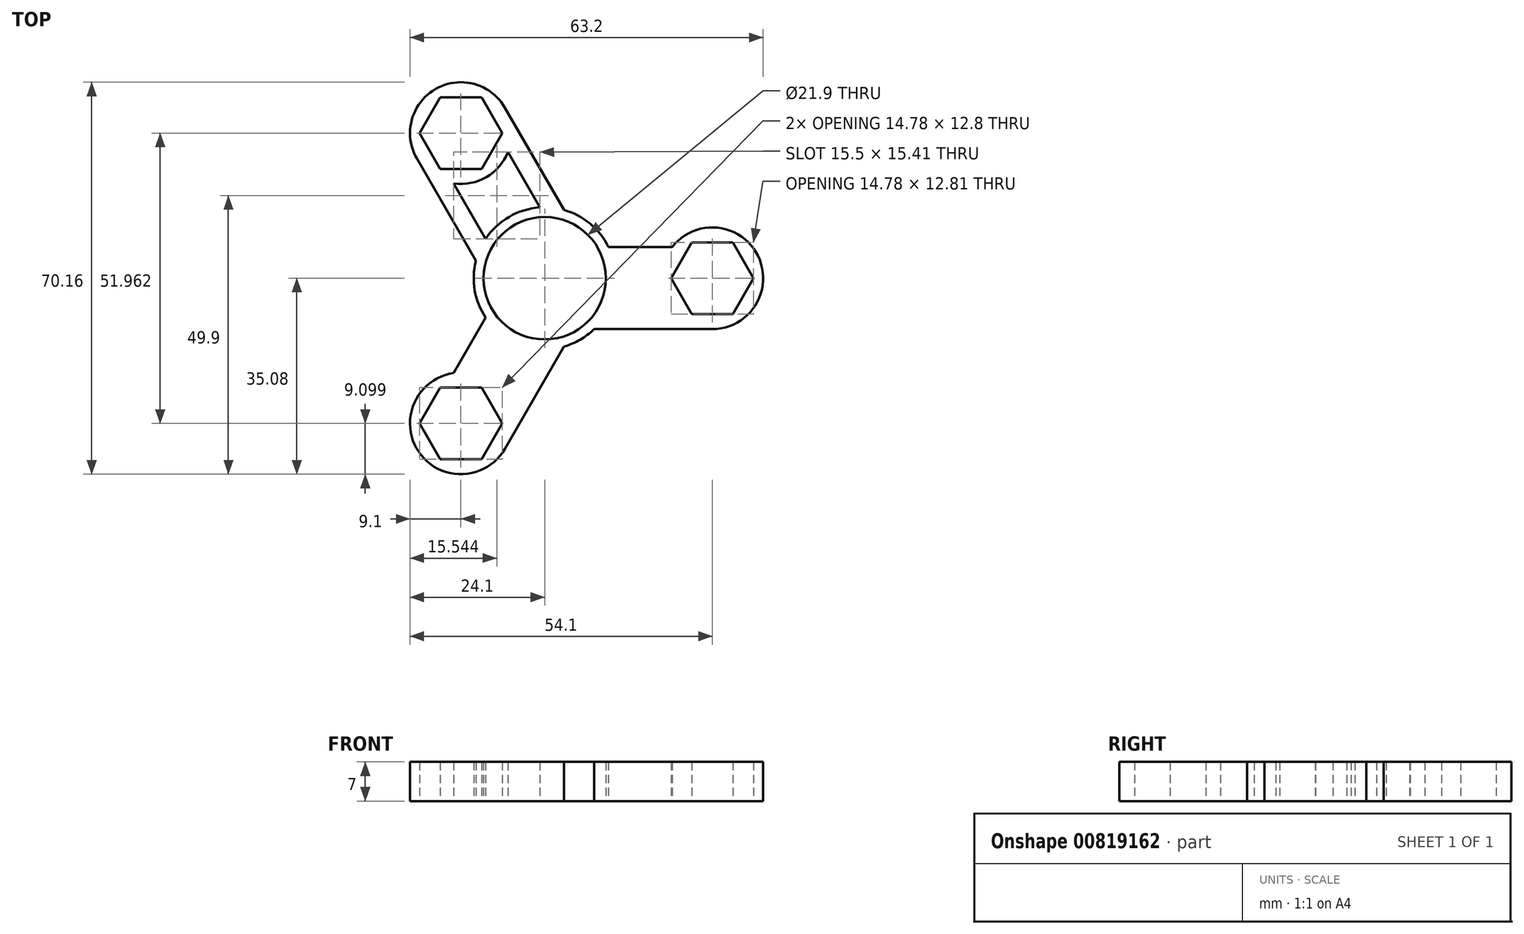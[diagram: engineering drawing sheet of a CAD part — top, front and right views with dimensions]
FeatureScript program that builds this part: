
annotation { "Feature Type Name" : "Feature", "Feature Type Description" : "" }
export const myFeature = defineFeature(function(context is Context, id is Id, definition is map)
    precondition{}
    {
        {
            var Q0;
            Q0=qCreatedBy(makeId("Top.planeOp"),FACE);
            var sketch = newSketch(context, id + "F0", { "sketchPlane" : qUnion([Q0])});
            skCircle(sketch, "E0", {"center": v(0, 0) * mm, "radius": 10.95 * mm});
            skCircle(sketch, "E1", {"center": v(0, 0) * mm, "radius": 12.7 * mm});
            skLineSegment(sketch, "E2", {"start": v(0, 0) * mm, "end": v(30, 0) * mm, "construction": true});
            skLineSegment(sketch, "E3", {"start": v(0, 0) * mm, "end": v(-15, -25.98) * mm, "construction": true});
            skLineSegment(sketch, "E4", {"start": v(0, 0) * mm, "end": v(-15, 25.98) * mm, "construction": true});
            skCircle(sketch, "E5.cCircle", {"center": v(-15, 25.98) * mm, "radius": 6.4 * mm, "construction": true});
            skLineSegment(sketch, "E5.0", {"start": v(-11.3, 32.38) * mm, "end": v(-7.6, 25.98) * mm});
            skLineSegment(sketch, "E5.1", {"start": v(-7.6, 25.98) * mm, "end": v(-11.3, 19.58) * mm});
            skLineSegment(sketch, "E5.2", {"start": v(-11.3, 19.58) * mm, "end": v(-18.7, 19.58) * mm});
            skLineSegment(sketch, "E5.3", {"start": v(-18.7, 19.58) * mm, "end": v(-22.4, 25.98) * mm});
            skLineSegment(sketch, "E5.4", {"start": v(-22.4, 25.98) * mm, "end": v(-18.7, 32.38) * mm});
            skLineSegment(sketch, "E5.5", {"start": v(-18.7, 32.38) * mm, "end": v(-11.3, 32.38) * mm});
            skPoint(sketch, "E5.0.midPoint", {"position": v(-9.46, 29.18) * mm});
            skCircle(sketch, "E6.cCircle", {"center": v(30, 0) * mm, "radius": 6.4 * mm, "construction": true});
            skLineSegment(sketch, "E6.0", {"start": v(26.3, -6.4) * mm, "end": v(22.6, 0.01) * mm});
            skLineSegment(sketch, "E6.1", {"start": v(22.6, 0.01) * mm, "end": v(26.32, 6.4) * mm});
            skLineSegment(sketch, "E6.2", {"start": v(26.32, 6.4) * mm, "end": v(33.7, 6.4) * mm});
            skLineSegment(sketch, "E6.3", {"start": v(33.7, 6.4) * mm, "end": v(37.4, -0.01) * mm});
            skLineSegment(sketch, "E6.4", {"start": v(37.4, -0.01) * mm, "end": v(33.68, -6.4) * mm});
            skLineSegment(sketch, "E6.5", {"start": v(33.68, -6.4) * mm, "end": v(26.3, -6.4) * mm});
            skPoint(sketch, "E6.0.midPoint", {"position": v(24.45, -3.19) * mm});
            skCircle(sketch, "E7.cCircle", {"center": v(-15, -25.98) * mm, "radius": 6.4 * mm, "construction": true});
            skLineSegment(sketch, "E7.0", {"start": v(-11.3, -19.58) * mm, "end": v(-7.6, -25.98) * mm});
            skLineSegment(sketch, "E7.1", {"start": v(-7.6, -25.98) * mm, "end": v(-11.3, -32.38) * mm});
            skLineSegment(sketch, "E7.2", {"start": v(-11.3, -32.38) * mm, "end": v(-18.7, -32.38) * mm});
            skLineSegment(sketch, "E7.3", {"start": v(-18.7, -32.38) * mm, "end": v(-22.4, -25.98) * mm});
            skLineSegment(sketch, "E7.4", {"start": v(-22.4, -25.98) * mm, "end": v(-18.7, -19.58) * mm});
            skLineSegment(sketch, "E7.5", {"start": v(-18.7, -19.58) * mm, "end": v(-11.3, -19.58) * mm});
            skPoint(sketch, "E7.0.midPoint", {"position": v(-9.46, -22.78) * mm});
            skCircle(sketch, "E8", {"center": v(-15, 25.98) * mm, "radius": 9.1 * mm});
            skCircle(sketch, "E9", {"center": v(30, 0) * mm, "radius": 9.1 * mm});
            skCircle(sketch, "E10", {"center": v(-15, -25.98) * mm, "radius": 9.1 * mm});
            skLineSegment(sketch, "E11.bottom", {"start": v(0, 9.1) * mm, "end": v(1.21, 9.1) * mm});
            skLineSegment(sketch, "E11.top", {"start": v(0, -9.1) * mm, "end": v(30.02, -9.1) * mm});
            skLineSegment(sketch, "E11.left", {"start": v(0, 9.1) * mm, "end": v(0, -9.1) * mm});
            skLineSegment(sketch, "E12.bottom", {"start": v(-7.12, 30.53) * mm, "end": v(3.45, 12.22) * mm});
            skLineSegment(sketch, "E12.top", {"start": v(-22.9, 21.47) * mm, "end": v(-7.9, -4.52) * mm});
            skLineSegment(sketch, "E12.right", {"start": v(7.86, 4.58) * mm, "end": v(-7.9, -4.52) * mm});
            skLineSegment(sketch, "E13.bottom", {"start": v(-22.88, -21.43) * mm, "end": v(-7.77, 4.75) * mm});
            skLineSegment(sketch, "E13.top", {"start": v(-7.14, -30.57) * mm, "end": v(8, -4.35) * mm});
            skLineSegment(sketch, "E13.right", {"start": v(-7.77, 4.75) * mm, "end": v(8, -4.35) * mm});
            skPoint(sketch, "E14", {"position": v(-7.12, 30.53) * mm});
            skPoint(sketch, "E15", {"position": v(30, 9.1) * mm});
            skPoint(sketch, "E16", {"position": v(-22.88, -21.43) * mm});
            skLineSegment(sketch, "E17.0", {"start": v(-10.15, 28.78) * mm, "end": v(4.83, 2.83) * mm});
            skLineSegment(sketch, "E18.0", {"start": v(-19.87, 23.22) * mm, "end": v(-4.87, -2.77) * mm});
            skLineSegment(sketch, "E19.0", {"start": v(-19.85, -23.18) * mm, "end": v(-4.74, 3) * mm});
            skLineSegment(sketch, "E20.0", {"start": v(-10.17, -28.82) * mm, "end": v(4.96, -2.6) * mm});
            skLineSegment(sketch, "E21.0", {"start": v(0, -5.6) * mm, "end": v(30.02, -5.6) * mm});
            skLineSegment(sketch, "E22.0", {"start": v(0, 5.6) * mm, "end": v(30, 5.6) * mm});
            skLineSegment(sketch, "E23.trimOffspring", {"start": v(7.27, 5.6) * mm, "end": v(7.86, 4.58) * mm});
            skLineSegment(sketch, "E24.trimOffspring", {"start": v(5.25, 9.1) * mm, "end": v(30, 9.1) * mm});
            skPoint(sketch, "E25", {"position": v(-40.98, 12.7) * mm});
            skSolve(sketch);
        }
        {
            var Q0;
            Q0 = qSketchRegion(id + "F0", true);
            var Q1;
            {var subQ0=sQuery(id+"F0.wireOp",EDGE,"E17.0");var subQ1=sQuery(id+"F0.wireOp",EDGE,"E0");var subQ2=makeQuery(id+"F0.imprint","INTERSECT",VERTEX,{"derivedFrom":[subQ1,subQ0]});Q1=makeQuery(id+"F0.imprint","IMPRINT",FACE,{"disambiguationData":[TD([[makeQuery(id+"F0.imprint","IMPRINT",EDGE,{"disambiguationData":[TD([[subQ2,-1.0]])],"derivedFrom":subQ1}),-1.0]])]});}
            var Q2;
            {var subQ0=sQuery(id+"F0.wireOp",EDGE,"E22.0");var subQ1=sQuery(id+"F0.wireOp",EDGE,"E0");var subQ2=makeQuery(id+"F0.imprint","INTERSECT",VERTEX,{"derivedFrom":[subQ1,subQ0]});Q2=makeQuery(id+"F0.imprint","IMPRINT",FACE,{"disambiguationData":[TD([[makeQuery(id+"F0.imprint","IMPRINT",EDGE,{"disambiguationData":[TD([[subQ2,1.0]])],"derivedFrom":subQ1}),-1.0]])]});}
            var Q3;
            {var subQ0=sQuery(id+"F0.wireOp",EDGE,"E19.0");var subQ1=sQuery(id+"F0.wireOp",EDGE,"E0");var subQ2=makeQuery(id+"F0.imprint","INTERSECT",VERTEX,{"derivedFrom":[subQ1,subQ0]});Q3=makeQuery(id+"F0.imprint","IMPRINT",FACE,{"disambiguationData":[TD([[makeQuery(id+"F0.imprint","IMPRINT",EDGE,{"disambiguationData":[TD([[subQ2,-1.0]])],"derivedFrom":subQ1}),-1.0]])]});}
            var Q4;
            {var subQ1=sQuery(id+"F0.wireOp",EDGE,"E6.0");var subQ5=sQuery(id+"F0.wireOp",EDGE,"E6.1");var subQ6=makeQuery(id+"F0.imprint","INTERSECT",VERTEX,{"derivedFrom":[subQ1,subQ5]});Q4=makeQuery(id+"F0.imprint","IMPRINT",FACE,{"disambiguationData":[TD([[makeQuery(id+"F0.imprint","IMPRINT",EDGE,{"disambiguationData":[TD([[subQ6,1.0]])],"derivedFrom":subQ1}),1.0]])]});}
            var Q5;
            {var subQ5=sQuery(id+"F0.wireOp",EDGE,"E5.1");var subQ7=sQuery(id+"F0.wireOp",EDGE,"E5.2");var subQ8=makeQuery(id+"F0.imprint","INTERSECT",VERTEX,{"derivedFrom":[subQ5,subQ7]});Q5=makeQuery(id+"F0.imprint","IMPRINT",FACE,{"disambiguationData":[TD([[makeQuery(id+"F0.imprint","IMPRINT",EDGE,{"disambiguationData":[TD([[subQ8,1.0]])],"derivedFrom":subQ5}),1.0]])]});}
            var Q6;
            {var subQ1=sQuery(id+"F0.wireOp",EDGE,"E7.5");var subQ7=sQuery(id+"F0.wireOp",EDGE,"E7.0");var subQ8=makeQuery(id+"F0.imprint","INTERSECT",VERTEX,{"derivedFrom":[subQ7,subQ1]});Q6=makeQuery(id+"F0.imprint","IMPRINT",FACE,{"disambiguationData":[TD([[makeQuery(id+"F0.imprint","IMPRINT",EDGE,{"disambiguationData":[TD([[subQ8,-1.0]])],"derivedFrom":subQ7}),1.0]])]});}
            extrude(context, id + "F1", {"entities" : qUnion([Q0, Q1, Q2, Q3, Q4, Q5, Q6]), "depth" : 7 * mm, "offsetDistance" : 25 * mm});
        }
    });
